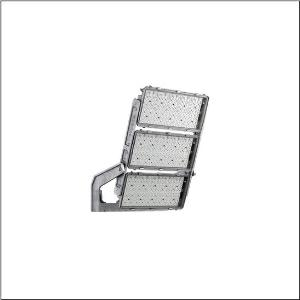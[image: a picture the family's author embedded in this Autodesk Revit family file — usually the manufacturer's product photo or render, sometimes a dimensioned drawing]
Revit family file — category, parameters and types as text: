
# Revit family: floodlight_fl_11_maxi_pro_remote___pl43_5xa779427a01aa_51b3
name_source: partatom
category: Lighting Fixtures
units: mm (PartAtom-declared; Revit-internal decimal feet)

## family parameters
Cut with Voids When Loaded = No
Host = Face
Light Source = No
Part Type = Normal
Room Calculation Point = No
Round Connector Dimension = Use Diameter
Shared = No

## types (1)
- --- (1 x LED, 177380 lm, 1425.5 W, 5000K)
    Apparent Load = 1425 VA
    CIE Flux Codes = 25 74 99 100 100
    Color Rendering = 70
    Color Temperature = 5000K
    Default Elevation = 1800 mm
    Description = Floodlight FL 11  maxi  pro Remote floodlight; light control with lens of PMMA; cover panel of toughened safety glass, transparent; light distribution: PL43, asymmetric direct distribution, LEDcolour temperature: 5000K, rated luminous flux: 177.380lm, colour rendering: CRI > 70, light colour: 750; luminous efficacy: 124lm/W; brightness control: DALI 2 (1 DALI address); with terminal, 8-pole, max. 2.5mm², mains connection: 220..240V/380..400V AC, 50/60Hz, surge voltage resistance: line to ground: 10kV, ECG replaceable separately, LED unit replaceable without ESD environment, dustproof LED module, dimming range 10..100%, no afterglow with DALI off / DMX off command; 1426W floodlight with 2x LED unit of diecast aluminium, coated grey; length: 713mm / width: 651mm / height: 338mm; mounting bracket, of diecast aluminium, uncoated, natural, equipment: Power, protection rating (complete): IP66; insulation class (complete): insulation class I (protective earthing); certification: CE, ENEC, VDE; ball protection: ball impact resistance with accessories, impact resistance: IK07; rated ambient temperature 10°C, only for outdoor installations, permissible operating ambient temperature: -40..+30°C, permissible storage temperature: -40..+85°C; packaging unit: 1 piece

Light Distribution: PL43
    Height = 320 mm
    Lamp = 1 x LED
    Lamp Light Flux = 177380 lm
    Lamp Power = 1425.5 W
    Lamp count = 1
    Length = 1002 mm
    Luminous efficacy = 124 lm/W
    Manufacturer = Siteco
    ModVariant = No
    Model = 5XA779427A01AA
    Mounting Place = Ceiling
    Mounting Type = Surface mounted
    Number of Poles = 1
    OnlyDefault = Yes
    Power Factor = 1
    Product Name = Floodlight FL 11 maxi pro Remote | PL43
    Product group = floodlight | ceiling mounted
    ProductGroupID = 303
    Protection Class = Protection class I
    Protection Degree = IP 66
    RLX_Detail_Level = 1
    RLX_Emergency_Light_Flux = 0 lm
    RLX_Emergency_Type = 0
    RLX_Emergency_Type_DB = No
    RlxData = <blob elided: 52609 chars, md5=34c6a04e>
    Socket = socket
    Standby Power = 0 W
    System Light Flux = 177380 lm
    System Power = 1425 W
    Type Comments = factory setting: luminous flux: 100 % | dim-lin: 254 | 980 mA
    Type Image = l_1006784.jpg
    URL = http://relux.com
    VarID = @adj_045047
    Voltage = 0 V
    Weight = 0.00 kg
    Width = 655 mm

## geometry (parser evidence)
native form markers: Blend x4, Sweep x15
no freeform markers — native parametric forms only
